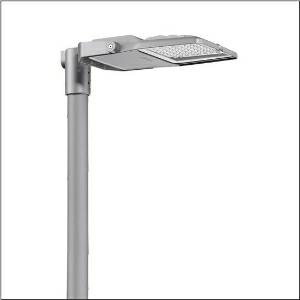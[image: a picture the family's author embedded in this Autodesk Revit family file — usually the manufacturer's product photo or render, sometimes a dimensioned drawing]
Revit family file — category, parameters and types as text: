
# Revit family: floodlight_fl_21_iq_mini___pl52_5xa7772d4d3a_25ab
name_source: partatom
category: Lighting Fixtures
units: mm (PartAtom-declared; Revit-internal decimal feet)

## family parameters
Cut with Voids When Loaded = No
Host = Face
Light Source = No
Part Type = Normal
Room Calculation Point = No
Round Connector Dimension = Use Diameter
Shared = No

## types (1)
- --- (1 x LED, 18610 lm, 143 W, 4000K)
    Apparent Load = 143 VA
    CIE Flux Codes = 26 60 98 100 100
    Color Rendering = 70
    Color Temperature = 4000K
    Default Elevation = 1800 mm
    Description = Floodlight FL 21 iQ mini, floodlight, primary light control with lens, of PMMA, primary optical cover: protective disc, of toughened safety glass, transparent, light distribution: PL52, light emission: direct distribution, installation type: surface-mounted, lamps: LED, High Power LED, rated values: 18.610lm | 143W | 130,1lm/W (begin service life); end service life: 18.610lm | 151,6W; at 50% lumin. flux: 9.305lm | 60,8W | 153lm/W, colour temperature: 4000K, colour rendering: CRI > 70, light colour: 740, light setting 1 begin service life: 100% | 18.610lm | 143W | 130,1lm/W | 4.000K, light setting 1 end service life: 151,6W, further light settings possible, control: pre-setting: linear dimming characteristic, Auto-Match, Temp-Guard, Night-Set, Smart-Wire, Desk-Remote (wireless, voltage-free reading and setting of iQ features in the workshop via application-optimized NFC function/RFID function), optimised constant luminous flux control (CLO 2.0), Light-Fading, Lumen-Switch, with terminal, 6-pole, mains connection: 220..240V, AC, 50/60Hz, luminaire housing, of diecast aluminium, powder-coated, SITECO metallic grey (DB 702S), corrosivity category C5 mid according to DIN EN ISO 12944suitable for swimming poolschlorine-resistant, sealing non-destructively replaceable, please order mast flange separately, mast bracket, of steel, galvanised, powder-coated, protection rating (complete): IP66, insulation class (complete): insulation class II (safety insulation), certification: CE, ENEC, VDE, protection symbol: D, impact resistance: IK08, permissible operating ambient temperature: -40..+40°C, permissible operating ambient temperature for outdoor applications: -40..+50°C, standard: DIN EN 12944, LABS conformity tested according to VDMA 24364:2018-05, packaging unit: 1 piece

Light Distribution: PL52
    Height = 70 mm
    Lamp = 1 x LED
    Lamp Light Flux = 18610 lm
    Lamp Power = 143 W
    Lamp count = 1
    Length = 485 mm
    Luminous efficacy = 130 lm/W
    Manufacturer = Siteco
    ModVariant = No
    Model = 5XA7772D4D3A
    Number of Poles = 1
    OnlyDefault = Yes
    Power Factor = 1
    Product Name = Floodlight FL 21 iQ mini | PL52
    Product group = floodlight | pylon annexe
    ProductGroupID = 6201
    Protection Class = Protection class II
    Protection Degree = IP 66
    RLX_Detail_Level = 1
    RLX_Emergency_Light_Flux = 0 lm
    RLX_Emergency_Type = 0
    RLX_Emergency_Type_DB = No
    RlxData = <blob elided: 101941 chars, md5=88c5c271>
    Socket = socket
    Standby Power = 0 W
    System Light Flux = 18610 lm
    System Power = 143 W
    Type Comments = factory setting: luminous flux: 100 % | dim-lin: 254 | 730 mA
    Type Image = l_1007125.jpg
    URL = http://relux.com
    VarID = @adj_163029
    Voltage = 0 V
    Weight = 0.00 kg
    Width = 337 mm

## geometry (parser evidence)
native form markers: Blend x4, Sweep x12
no freeform markers — native parametric forms only
